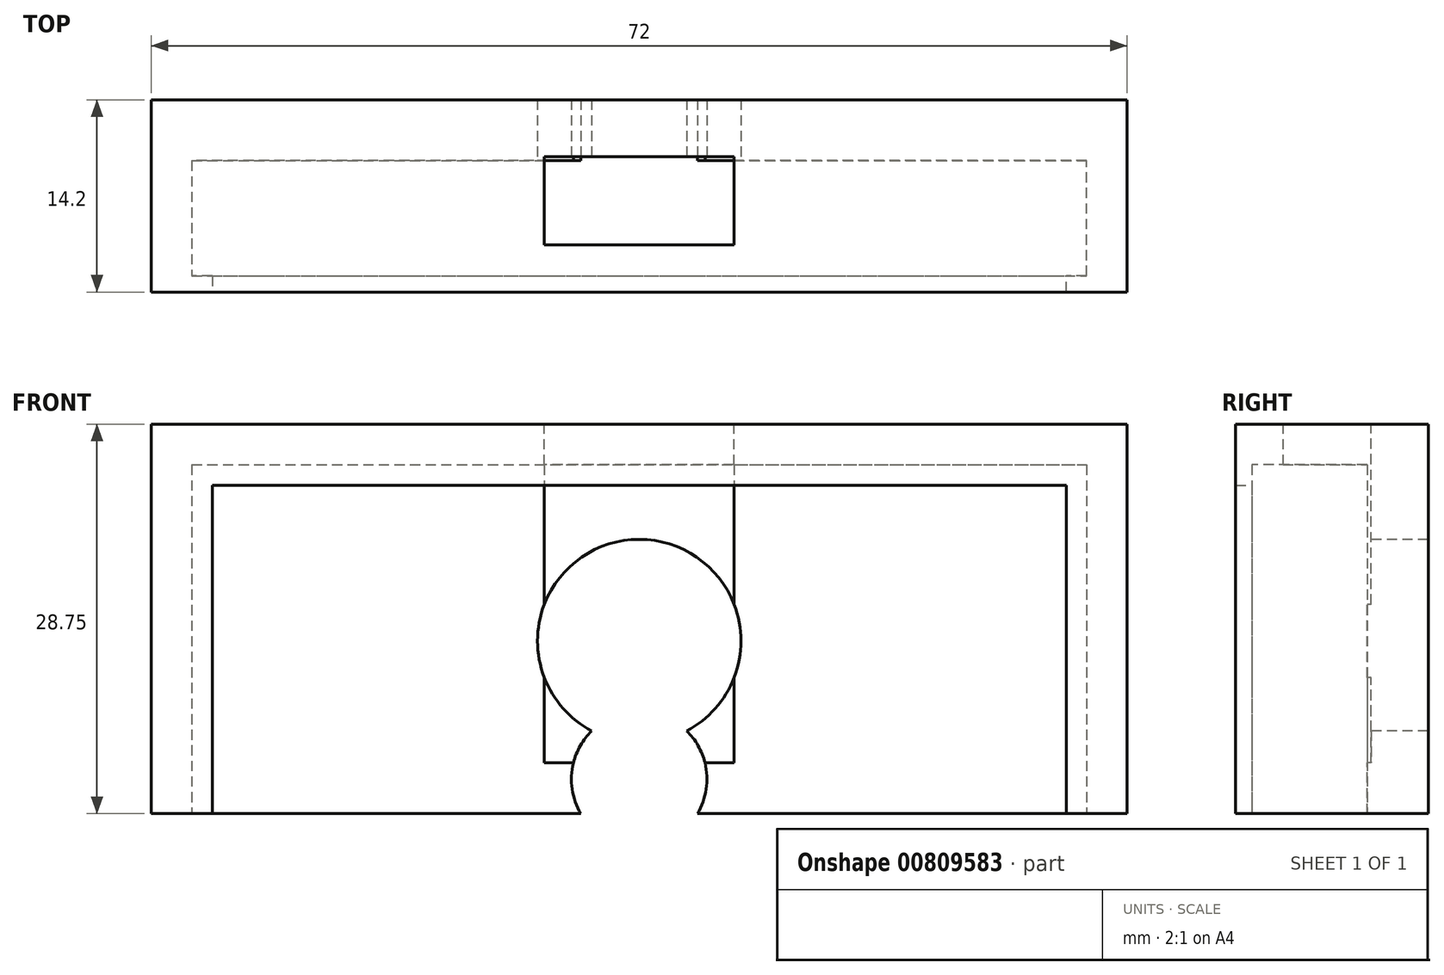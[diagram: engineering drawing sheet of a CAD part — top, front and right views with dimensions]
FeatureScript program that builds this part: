
annotation { "Feature Type Name" : "Feature", "Feature Type Description" : "" }
export const myFeature = defineFeature(function(context is Context, id is Id, definition is map)
    precondition{}
    {
        {
            var Q0;
            Q0=qCreatedBy(makeId("Front.planeOp"),FACE);
            var sketch = newSketch(context, id + "F0", { "sketchPlane" : qUnion([Q0])});
            skPoint(sketch, "E0.0", {"position": v(0, 0) * mm});
            skLineSegment(sketch, "E1.bottom", {"start": v(-36, 66) * mm, "end": v(36, 66) * mm});
            skLineSegment(sketch, "E1.top", {"start": v(-36, -66) * mm, "end": v(36, -66) * mm});
            skLineSegment(sketch, "E1.left", {"start": v(-36, 66) * mm, "end": v(-36, -66) * mm});
            skLineSegment(sketch, "E1.right", {"start": v(36, 66) * mm, "end": v(36, -66) * mm});
            skSolve(sketch);
        }
        {
            var Q0;
            Q0=makeQuery(id+"F0.imprint","IMPRINT",FACE,{"disambiguationData":[TD([[makeQuery(id+"F0.imprint","IMPRINT",EDGE,{"derivedFrom":sQuery(id+"F0.wireOp",EDGE,"E1.bottom")}),-1.0]])]});
            extrude(context, id + "F1", {"entities" : qUnion([Q0]), "depth" : 13 * mm, "offsetDistance" : 25 * mm});
        }
        {
            var Q0;
            Q0=makeQuery(id+"F1.opExtrude","CAP_FACE",FACE,{"disambiguationData":[OSD([sQuery(id+"F0.wireOp",EDGE,"E1.bottom"),sQuery(id+"F0.wireOp",EDGE,"E1.top"),sQuery(id+"F0.wireOp",EDGE,"E1.left"),sQuery(id+"F0.wireOp",EDGE,"E1.right")])],"isStart":false});
            var sketch = newSketch(context, id + "F2", { "sketchPlane" : qUnion([Q0])});
            skLineSegment(sketch, "E2.bottom", {"start": v(-33, 63) * mm, "end": v(33, 63) * mm});
            skLineSegment(sketch, "E2.top", {"start": v(-33, -63) * mm, "end": v(33, -63) * mm});
            skLineSegment(sketch, "E2.left", {"start": v(-33, 63) * mm, "end": v(-33, -63) * mm});
            skLineSegment(sketch, "E2.right", {"start": v(33, 63) * mm, "end": v(33, -63) * mm});
            skSolve(sketch);
        }
        {
            var Q0;
            Q0=makeQuery(id+"F2.imprint","IMPRINT",FACE,{"disambiguationData":[TD([[makeQuery(id+"F2.imprint","IMPRINT",EDGE,{"derivedFrom":sQuery(id+"F2.wireOp",EDGE,"E2.bottom")}),-1.0]])]});
            extrude(context, id + "F3", {"entities" : qUnion([Q0]), "operationType" : NewBodyOperationType.REMOVE, "oppositeDirection" : true, "depth" : 8.5 * mm, "offsetDistance" : 25 * mm});
        }
        {
            var Q0;
            Q0=makeQuery(id+"F1.opExtrude","CAP_FACE",FACE,{"disambiguationData":[OSD([sQuery(id+"F0.wireOp",EDGE,"E1.bottom"),sQuery(id+"F0.wireOp",EDGE,"E1.top"),sQuery(id+"F0.wireOp",EDGE,"E1.left"),sQuery(id+"F0.wireOp",EDGE,"E1.right")])],"isStart":false});
            var sketch = newSketch(context, id + "F4", { "sketchPlane" : qUnion([Q0])});
            skLineSegment(sketch, "E3.bottom", {"start": v(-31.5, 61.5) * mm, "end": v(31.5, 61.5) * mm});
            skLineSegment(sketch, "E3.top", {"start": v(-31.5, -61.5) * mm, "end": v(31.5, -61.5) * mm});
            skLineSegment(sketch, "E3.left", {"start": v(-31.5, 61.5) * mm, "end": v(-31.5, -61.5) * mm});
            skLineSegment(sketch, "E3.right", {"start": v(31.5, 61.5) * mm, "end": v(31.5, -61.5) * mm});
            skSolve(sketch);
        }
        {
            var Q0;
            Q0=makeQuery(id+"F4.imprint","IMPRINT",FACE,{"disambiguationData":[TD([[makeQuery(id+"F4.imprint","IMPRINT",EDGE,{"derivedFrom":sQuery(id+"F4.wireOp",EDGE,"E3.bottom")}),1.0]])]});
            var Q1;
            Q1=makeQuery(id+"F4.imprint","IMPRINT",FACE,{"disambiguationData":[TD([[makeQuery(id+"F4.imprint","IMPRINT",EDGE,{"derivedFrom":makeQuery(id+"F1.opExtrude","CAP_EDGE",EDGE,{"disambiguationData":[OSD([sQuery(id+"F0.wireOp",EDGE,"E1.bottom")])],"isStart":false})}),-1.0]])]});
            extrude(context, id + "F5", {"entities" : qUnion([Q0, Q1]), "operationType" : NewBodyOperationType.ADD, "depth" : 1.2 * mm, "offsetDistance" : 25 * mm});
        }
        {
            var Q0;
            Q0=makeQuery(id+"F3.boolean.opBoolean","COPY",FACE,{"derivedFrom":makeQuery(id+"F3.opExtrude","CAP_FACE",FACE,{"disambiguationData":[OSD([sQuery(id+"F2.wireOp",EDGE,"E2.bottom"),sQuery(id+"F2.wireOp",EDGE,"E2.top"),sQuery(id+"F2.wireOp",EDGE,"E2.left"),sQuery(id+"F2.wireOp",EDGE,"E2.right")])],"isStart":false})});
            var sketch = newSketch(context, id + "F6", { "sketchPlane" : qUnion([Q0])});
            skCircle(sketch, "E4", {"center": v(0, 50) * mm, "radius": 7.5 * mm});
            skSolve(sketch);
        }
        {
            var Q0;
            Q0=makeQuery(id+"F6.imprint","IMPRINT",FACE,{"disambiguationData":[TD([[makeQuery(id+"F6.imprint","IMPRINT",EDGE,{"derivedFrom":sQuery(id+"F6.wireOp",EDGE,"E4")}),1.0]])]});
            extrude(context, id + "F7", {"entities" : qUnion([Q0]), "operationType" : NewBodyOperationType.REMOVE, "oppositeDirection" : true, "depth" : 25 * mm, "offsetDistance" : 25 * mm});
        }
        {
            var Q0;
            Q0=qSketchRegion(id+"F6",true);
            extrude(context, id + "F8", {"entities" : qUnion([Q0]), "operationType" : NewBodyOperationType.REMOVE, "oppositeDirection" : true, "depth" : 25 * mm, "offsetDistance" : 25 * mm});
        }
        {
            var Q0;
            Q0=makeQuery(id+"F3.boolean.opBoolean","COPY",FACE,{"derivedFrom":makeQuery(id+"F3.opExtrude","CAP_FACE",FACE,{"disambiguationData":[OSD([sQuery(id+"F2.wireOp",EDGE,"E2.bottom"),sQuery(id+"F2.wireOp",EDGE,"E2.top"),sQuery(id+"F2.wireOp",EDGE,"E2.left"),sQuery(id+"F2.wireOp",EDGE,"E2.right")])],"isStart":false})});
            var sketch = newSketch(context, id + "F9", { "sketchPlane" : qUnion([Q0])});
            skCircle(sketch, "E5", {"center": v(0, 39.8) * mm, "radius": 5 * mm});
            skSolve(sketch);
        }
        {
            var Q0;
            Q0=qSketchRegion(id+"F9",true);
            extrude(context, id + "F10", {"entities" : qUnion([Q0]), "operationType" : NewBodyOperationType.REMOVE, "oppositeDirection" : true, "depth" : 25 * mm, "offsetDistance" : 25 * mm});
        }
        {
            var Q0;
            {var subQ0=sQuery(id+"F0.wireOp",EDGE,"E1.bottom");Q0=makeQuery(id+"F5.boolean.opBoolean","MERGE",FACE,{"derivedFrom":[makeQuery(id+"F1.opExtrude","SWEPT_FACE",FACE,{"disambiguationData":[OSD([subQ0])]}),makeQuery(id+"F5.opExtrude","SWEPT_FACE",FACE,{"disambiguationData":[OSD([subQ0])]})]});}
            var sketch = newSketch(context, id + "F11", { "sketchPlane" : qUnion([Q0])});
            skLineSegment(sketch, "E6.bottom", {"start": v(-7, -4.2) * mm, "end": v(7, -4.2) * mm});
            skLineSegment(sketch, "E6.top", {"start": v(-7, -10.7) * mm, "end": v(7, -10.7) * mm});
            skLineSegment(sketch, "E6.left", {"start": v(-7, -4.2) * mm, "end": v(-7, -10.7) * mm});
            skLineSegment(sketch, "E6.right", {"start": v(7, -4.2) * mm, "end": v(7, -10.7) * mm});
            skSolve(sketch);
        }
        {
            var Q0;
            Q0=qSketchRegion(id+"F11",true);
            extrude(context, id + "F12", {"entities" : qUnion([Q0]), "operationType" : NewBodyOperationType.REMOVE, "oppositeDirection" : true, "depth" : 25 * mm, "offsetDistance" : 25 * mm});
        }
        {
            var Q0;
            Q0=makeQuery(id+"F3.boolean.opBoolean","COPY",FACE,{"derivedFrom":makeQuery(id+"F3.opExtrude","CAP_FACE",FACE,{"disambiguationData":[OSD([sQuery(id+"F2.wireOp",EDGE,"E2.bottom"),sQuery(id+"F2.wireOp",EDGE,"E2.top"),sQuery(id+"F2.wireOp",EDGE,"E2.left"),sQuery(id+"F2.wireOp",EDGE,"E2.right")])],"isStart":false})});
            var sketch = newSketch(context, id + "F13", { "sketchPlane" : qUnion([Q0])});
            skLineSegment(sketch, "E7.bottom", {"start": v(-17.5, -52.5) * mm, "end": v(17.5, -52.5) * mm});
            skLineSegment(sketch, "E7.top", {"start": v(-17.5, -55.5) * mm, "end": v(17.5, -55.5) * mm});
            skLineSegment(sketch, "E7.left", {"start": v(-17.5, -52.5) * mm, "end": v(-17.5, -55.5) * mm});
            skLineSegment(sketch, "E7.right", {"start": v(17.5, -52.5) * mm, "end": v(17.5, -55.5) * mm});
            skSolve(sketch);
        }
        {
            var Q0;
            Q0=makeQuery(id+"F13.imprint","IMPRINT",FACE,{"disambiguationData":[TD([[makeQuery(id+"F13.imprint","IMPRINT",EDGE,{"derivedFrom":sQuery(id+"F13.wireOp",EDGE,"E7.bottom")}),-1.0]])]});
            extrude(context, id + "F14", {"entities" : qUnion([Q0]), "operationType" : NewBodyOperationType.REMOVE, "oppositeDirection" : true, "depth" : 25 * mm, "offsetDistance" : 25 * mm});
        }
        {
            var Q0;
            Q0=qCreatedBy(makeId("Front.planeOp"),FACE);
            var sketch = newSketch(context, id + "F15", { "sketchPlane" : qUnion([Q0])});
            skLineSegment(sketch, "E8.bottom", {"start": v(-51.41, 37.25) * mm, "end": v(44.05, 37.25) * mm});
            skLineSegment(sketch, "E8.top", {"start": v(-51.41, -70.4) * mm, "end": v(44.05, -70.4) * mm});
            skLineSegment(sketch, "E8.left", {"start": v(-51.41, 37.25) * mm, "end": v(-51.41, -70.4) * mm});
            skLineSegment(sketch, "E8.right", {"start": v(44.05, 37.25) * mm, "end": v(44.05, -70.4) * mm});
            skSolve(sketch);
        }
        {
            var Q0;
            Q0=makeQuery(id+"F15.imprint","IMPRINT",FACE,{"disambiguationData":[TD([[makeQuery(id+"F15.imprint","IMPRINT",EDGE,{"derivedFrom":sQuery(id+"F15.wireOp",EDGE,"E8.bottom")}),-1.0]])]});
            extrude(context, id + "F16", {"entities" : qUnion([Q0]), "operationType" : NewBodyOperationType.REMOVE, "endBound" : BoundingType.THROUGH_ALL, "depth" : 25 * mm, "offsetDistance" : 25 * mm});
        }
    });
